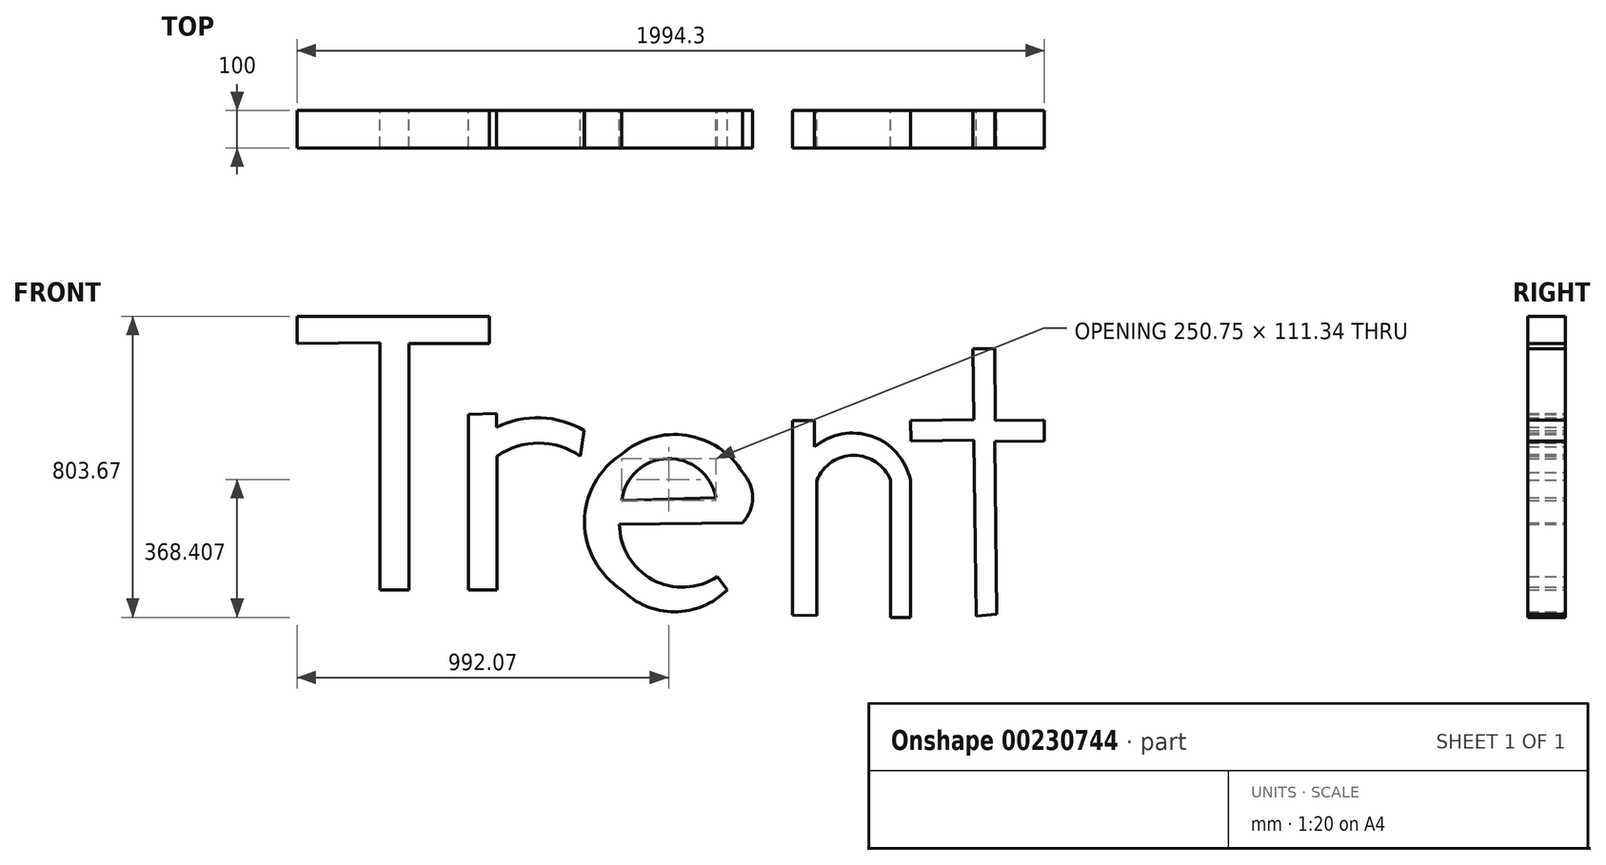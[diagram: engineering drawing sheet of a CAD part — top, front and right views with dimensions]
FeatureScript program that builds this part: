
annotation { "Feature Type Name" : "Feature", "Feature Type Description" : "" }
export const myFeature = defineFeature(function(context is Context, id is Id, definition is map)
    precondition{}
    {
        {
            var Q0;
            Q0=qCreatedBy(makeId("Front.planeOp"),FACE);
            var sketch = newSketch(context, id + "F0", { "sketchPlane" : qUnion([Q0])});
            skLineSegment(sketch, "E0", {"start": v(-1036.08, -451.63) * mm, "end": v(-1036.08, 208.1) * mm});
            skLineSegment(sketch, "E1", {"start": v(-1036.08, -451.63) * mm, "end": v(-958.6, -451.63) * mm});
            skLineSegment(sketch, "E2", {"start": v(-958.6, -451.63) * mm, "end": v(-958.6, 205.24) * mm});
            skLineSegment(sketch, "E3", {"start": v(-958.6, 205.24) * mm, "end": v(-744.17, 205.24) * mm});
            skLineSegment(sketch, "E4", {"start": v(-744.17, 205.24) * mm, "end": v(-744.17, 278.19) * mm});
            skLineSegment(sketch, "E5", {"start": v(-744.17, 278.19) * mm, "end": v(-1257.02, 278.19) * mm});
            skLineSegment(sketch, "E6", {"start": v(-1257.02, 278.19) * mm, "end": v(-1257.02, 205.24) * mm});
            skLineSegment(sketch, "E7", {"start": v(-1257.02, 205.24) * mm, "end": v(-1036.08, 208.1) * mm});
            skLineSegment(sketch, "E8", {"start": v(-799.98, -451.63) * mm, "end": v(-799.98, 16.85) * mm});
            skLineSegment(sketch, "E9", {"start": v(-799.98, -451.63) * mm, "end": v(-723.04, -451.63) * mm});
            skLineSegment(sketch, "E10", {"start": v(-723.04, -451.63) * mm, "end": v(-723.04, -94.9) * mm});
            skArc(sketch, "E11", {"start": v(-490.38, -27.12) * mm, "mid": v(-606.44, 7.77) * mm, "end": v(-724.87, -17.96) * mm});
            skArc(sketch, "E12", {"start": v(-501.37, -94.9) * mm, "mid": v(-612.2, -60.1) * mm, "end": v(-723.04, -94.9) * mm});
            skLineSegment(sketch, "E13", {"start": v(-501.37, -94.9) * mm, "end": v(-490.38, -27.12) * mm});
            skLineSegment(sketch, "E14", {"start": v(-724.87, -17.96) * mm, "end": v(-724.87, 18.68) * mm});
            skLineSegment(sketch, "E15", {"start": v(-799.98, 16.85) * mm, "end": v(-724.87, 18.68) * mm});
            skArc(sketch, "E16", {"start": v(-390.32, -451.63) * mm, "mid": v(-249.53, -510.33) * mm, "end": v(-108.75, -451.63) * mm});
            skPoint(sketch, "E16.startSnap0", {"position": v(-761.5, -451.63) * mm});
            skPoint(sketch, "E16.endSnap0", {"position": v(-761.5, -451.63) * mm});
            skArc(sketch, "E17", {"start": v(-390.32, -89.42) * mm, "mid": v(-489.45, -270.52) * mm, "end": v(-390.32, -451.63) * mm});
            skArc(sketch, "E18", {"start": v(-67.64, -138.75) * mm, "mid": v(-217.58, -39.51) * mm, "end": v(-390.32, -89.42) * mm});
            skArc(sketch, "E19", {"start": v(-67.64, -272.35) * mm, "mid": v(-41.4, -205.55) * mm, "end": v(-67.64, -138.75) * mm});
            skLineSegment(sketch, "E20", {"start": v(-108.75, -451.63) * mm, "end": v(-135.46, -416.22) * mm});
            skArc(sketch, "E21", {"start": v(-396.5, -276.46) * mm, "mid": v(-307.96, -424.74) * mm, "end": v(-135.46, -416.22) * mm});
            skLineSegment(sketch, "E22", {"start": v(-396.5, -276.46) * mm, "end": v(-67.64, -272.35) * mm});
            skArc(sketch, "E23", {"start": v(-139.57, -205.55) * mm, "mid": v(-268.04, -101.4) * mm, "end": v(-390.32, -212.74) * mm});
            skLineSegment(sketch, "E24", {"start": v(-390.32, -212.74) * mm, "end": v(-139.57, -205.55) * mm});
            skLineSegment(sketch, "E25", {"start": v(65.58, -519.13) * mm, "end": v(65.58, 0) * mm});
            skLineSegment(sketch, "E26", {"start": v(65.58, -519.13) * mm, "end": v(130.61, -520.93) * mm});
            skLineSegment(sketch, "E27", {"start": v(130.61, -520.93) * mm, "end": v(130.61, -159.02) * mm});
            skArc(sketch, "E28", {"start": v(327.33, -159.02) * mm, "mid": v(228.97, -92.83) * mm, "end": v(130.61, -159.02) * mm});
            skLineSegment(sketch, "E29", {"start": v(327.33, -159.02) * mm, "end": v(327.33, -525.48) * mm});
            skLineSegment(sketch, "E30", {"start": v(327.33, -525.48) * mm, "end": v(379.68, -525.48) * mm});
            skLineSegment(sketch, "E31", {"start": v(379.68, -525.48) * mm, "end": v(379.68, -159.02) * mm});
            skArc(sketch, "E32", {"start": v(379.68, -159.02) * mm, "mid": v(277.28, -41.87) * mm, "end": v(124.27, -70.18) * mm});
            skLineSegment(sketch, "E33", {"start": v(124.27, -70.18) * mm, "end": v(124.27, 0) * mm});
            skLineSegment(sketch, "E34", {"start": v(124.27, 0) * mm, "end": v(65.58, 0) * mm});
            skLineSegment(sketch, "E35", {"start": v(555.36, -521.35) * mm, "end": v(549.5, -51.94) * mm});
            skLineSegment(sketch, "E36", {"start": v(549.5, -51.94) * mm, "end": v(381.01, -54.04) * mm});
            skLineSegment(sketch, "E37", {"start": v(381.01, -54.04) * mm, "end": v(380.34, 0) * mm});
            skLineSegment(sketch, "E38", {"start": v(380.34, 0) * mm, "end": v(549.5, 2.11) * mm});
            skLineSegment(sketch, "E39", {"start": v(549.5, 2.11) * mm, "end": v(547.13, 191.73) * mm});
            skLineSegment(sketch, "E40", {"start": v(547.13, 191.73) * mm, "end": v(604.59, 192.45) * mm});
            skLineSegment(sketch, "E41", {"start": v(604.59, 192.45) * mm, "end": v(607, 0) * mm});
            skLineSegment(sketch, "E42", {"start": v(607, 0) * mm, "end": v(736.59, 1.62) * mm});
            skLineSegment(sketch, "E43", {"start": v(736.59, 1.62) * mm, "end": v(737.28, -54.04) * mm});
            skLineSegment(sketch, "E44", {"start": v(737.28, -54.04) * mm, "end": v(604.59, -55.7) * mm});
            skLineSegment(sketch, "E45", {"start": v(604.59, -55.7) * mm, "end": v(610.35, -517.06) * mm});
            skLineSegment(sketch, "E46", {"start": v(610.35, -517.06) * mm, "end": v(555.36, -521.35) * mm});
            skSolve(sketch);
        }
        {
            var Q0;
            Q0=makeQuery(id+"F0.imprint","IMPRINT",FACE,{"disambiguationData":[TD([[makeQuery(id+"F0.imprint","IMPRINT",EDGE,{"derivedFrom":sQuery(id+"F0.wireOp",EDGE,"E0")}),-1.0]])]});
            extrude(context, id + "F1", {"entities" : qUnion([Q0]), "depth" : 100 * mm});
        }
        {
            var Q0;
            Q0=makeQuery(id+"F0.imprint","IMPRINT",FACE,{"disambiguationData":[TD([[makeQuery(id+"F0.imprint","IMPRINT",EDGE,{"derivedFrom":sQuery(id+"F0.wireOp",EDGE,"E8")}),-1.0]])]});
            extrude(context, id + "F2", {"entities" : qUnion([Q0]), "depth" : 100 * mm});
        }
        {
            var Q0;
            Q0=makeQuery(id+"F0.imprint","IMPRINT",FACE,{"disambiguationData":[TD([[makeQuery(id+"F0.imprint","IMPRINT",EDGE,{"derivedFrom":sQuery(id+"F0.wireOp",EDGE,"E16")}),1.0]])]});
            extrude(context, id + "F3", {"entities" : qUnion([Q0]), "depth" : 100 * mm});
        }
        {
            var Q0;
            Q0=makeQuery(id+"F0.imprint","IMPRINT",FACE,{"disambiguationData":[TD([[makeQuery(id+"F0.imprint","IMPRINT",EDGE,{"derivedFrom":sQuery(id+"F0.wireOp",EDGE,"E25")}),-1.0]])]});
            extrude(context, id + "F4", {"entities" : qUnion([Q0]), "depth" : 100 * mm});
        }
        {
            var Q0;
            Q0=makeQuery(id+"F0.imprint","IMPRINT",FACE,{"disambiguationData":[TD([[makeQuery(id+"F0.imprint","IMPRINT",EDGE,{"derivedFrom":sQuery(id+"F0.wireOp",EDGE,"E35")}),-1.0]])]});
            extrude(context, id + "F5", {"entities" : qUnion([Q0]), "depth" : 100 * mm});
        }
    });
